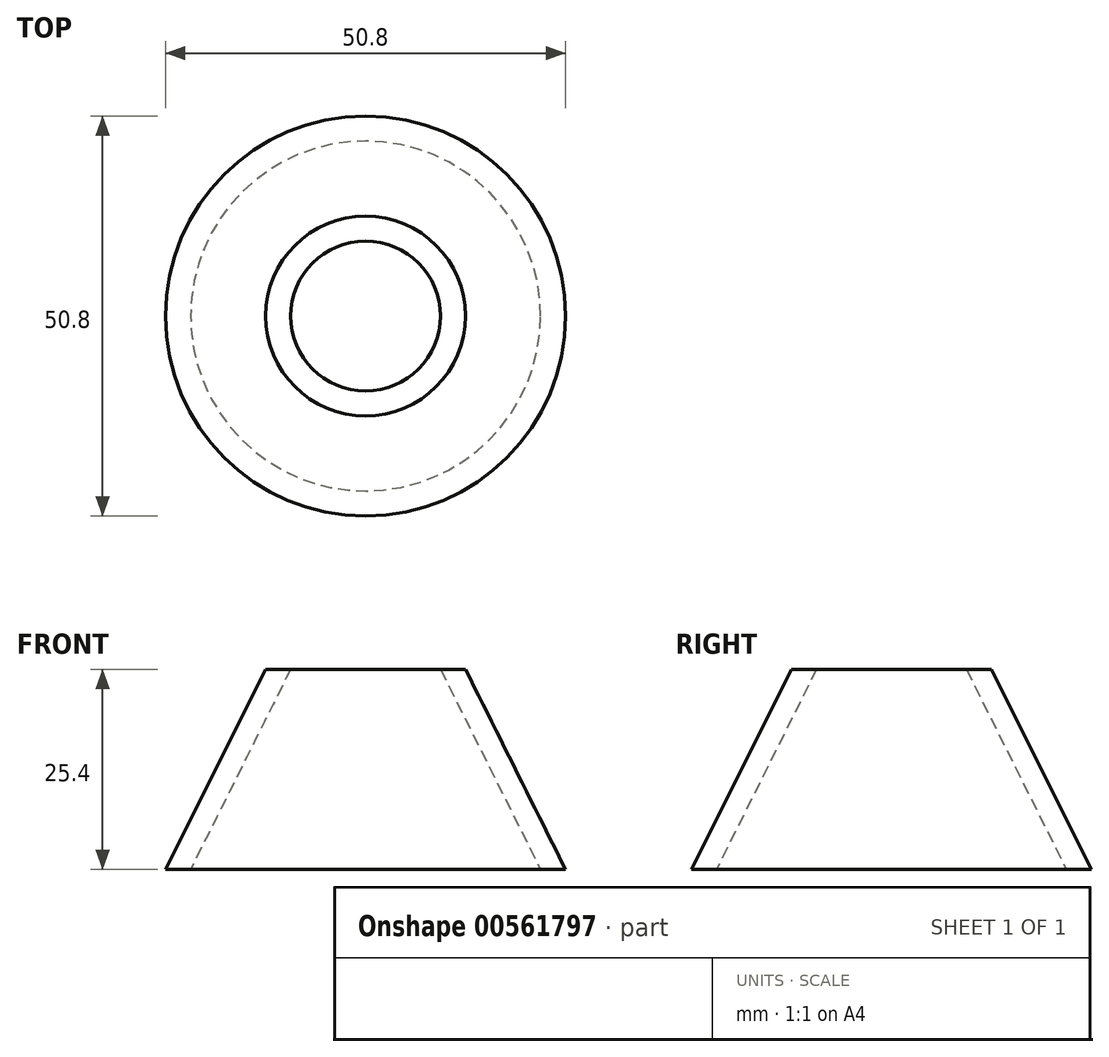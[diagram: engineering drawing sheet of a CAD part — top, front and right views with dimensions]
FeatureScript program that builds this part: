
annotation { "Feature Type Name" : "Feature", "Feature Type Description" : "" }
export const myFeature = defineFeature(function(context is Context, id is Id, definition is map)
    precondition{}
    {
        {
            var Q0;
            Q0=qCreatedBy(makeId("Top.planeOp"),FACE);
            cPlane(context, id + "F0", {"entities" : qUnion([Q0]), "cplaneType" : CPlaneType.OFFSET, "offset" : 25.4 * mm, "width" : 152.4 * mm, "height" : 152.4 * mm});
        }
        {
            var Q0;
            Q0=qCreatedBy(id+"F0.planeOp",FACE);
            var sketch = newSketch(context, id + "F1", { "sketchPlane" : qUnion([Q0])});
            skCircle(sketch, "E0", {"center": v(0, 0) * mm, "radius": 12.7 * mm});
            skSolve(sketch);
        }
        {
            var Q0;
            Q0=qCreatedBy(makeId("Top.planeOp"),FACE);
            var sketch = newSketch(context, id + "F2", { "sketchPlane" : qUnion([Q0])});
            skCircle(sketch, "E1", {"center": v(0, 0) * mm, "radius": 25.4 * mm});
            skSolve(sketch);
        }
        {
            var Q0;
            Q0=makeQuery(id+"F2.imprint","IMPRINT",FACE,{"disambiguationData":[TD([[makeQuery(id+"F2.imprint","IMPRINT",EDGE,{"derivedFrom":sQuery(id+"F2.wireOp",EDGE,"E1")}),1.0]])]});
            var Q1;
            Q1=makeQuery(id+"F1.imprint","IMPRINT",FACE,{"disambiguationData":[TD([[makeQuery(id+"F1.imprint","IMPRINT",EDGE,{"derivedFrom":sQuery(id+"F1.wireOp",EDGE,"E0")}),1.0]])]});
            loft(context, id + "F3", {"sheetProfilesArray" : [{ "sheetProfileEntities" : qUnion([Q0]) }, { "sheetProfileEntities" : qUnion([Q1]) }]});
        }
        {
            var Q0;
            Q0=makeQuery(id+"F3.opLoft","CAP_FACE",FACE,{"disambiguationData":[OSD([makeQuery(id+"F1.imprint","IMPRINT",FACE,{"disambiguationData":[TD([[makeQuery(id+"F1.imprint","IMPRINT",EDGE,{"derivedFrom":sQuery(id+"F1.wireOp",EDGE,"E0")}),1.0]])]})])],"isStart":true});
            var sketch = newSketch(context, id + "F4", { "sketchPlane" : qUnion([Q0])});
            skCircle(sketch, "E2", {"center": v(0, 0) * mm, "radius": 9.53 * mm});
            skSolve(sketch);
        }
        {
            var Q0;
            Q0=makeQuery(id+"F3.opLoft","CAP_FACE",FACE,{"disambiguationData":[OSD([makeQuery(id+"F2.imprint","IMPRINT",FACE,{"disambiguationData":[TD([[makeQuery(id+"F2.imprint","IMPRINT",EDGE,{"derivedFrom":sQuery(id+"F2.wireOp",EDGE,"E1")}),1.0]])]})])],"isStart":true});
            var sketch = newSketch(context, id + "F5", { "sketchPlane" : qUnion([Q0])});
            skCircle(sketch, "E3", {"center": v(0, 0) * mm, "radius": 22.23 * mm});
            skSolve(sketch);
        }
        {
            var Q1;
            Q1=makeQuery(id+"F5.imprint","IMPRINT",FACE,{"disambiguationData":[TD([[makeQuery(id+"F5.imprint","IMPRINT",EDGE,{"derivedFrom":sQuery(id+"F5.wireOp",EDGE,"E3")}),1.0]])]});
            var Q2;
            Q2=makeQuery(id+"F4.imprint","IMPRINT",FACE,{"disambiguationData":[TD([[makeQuery(id+"F4.imprint","IMPRINT",EDGE,{"derivedFrom":sQuery(id+"F4.wireOp",EDGE,"E2")}),1.0]])]});
            loft(context, id + "F6", {"operationType" : NewBodyOperationType.REMOVE, "sheetProfilesArray" : [{ "sheetProfileEntities" : qUnion([Q1]) }, { "sheetProfileEntities" : qUnion([Q2]) }]});
        }
    });
